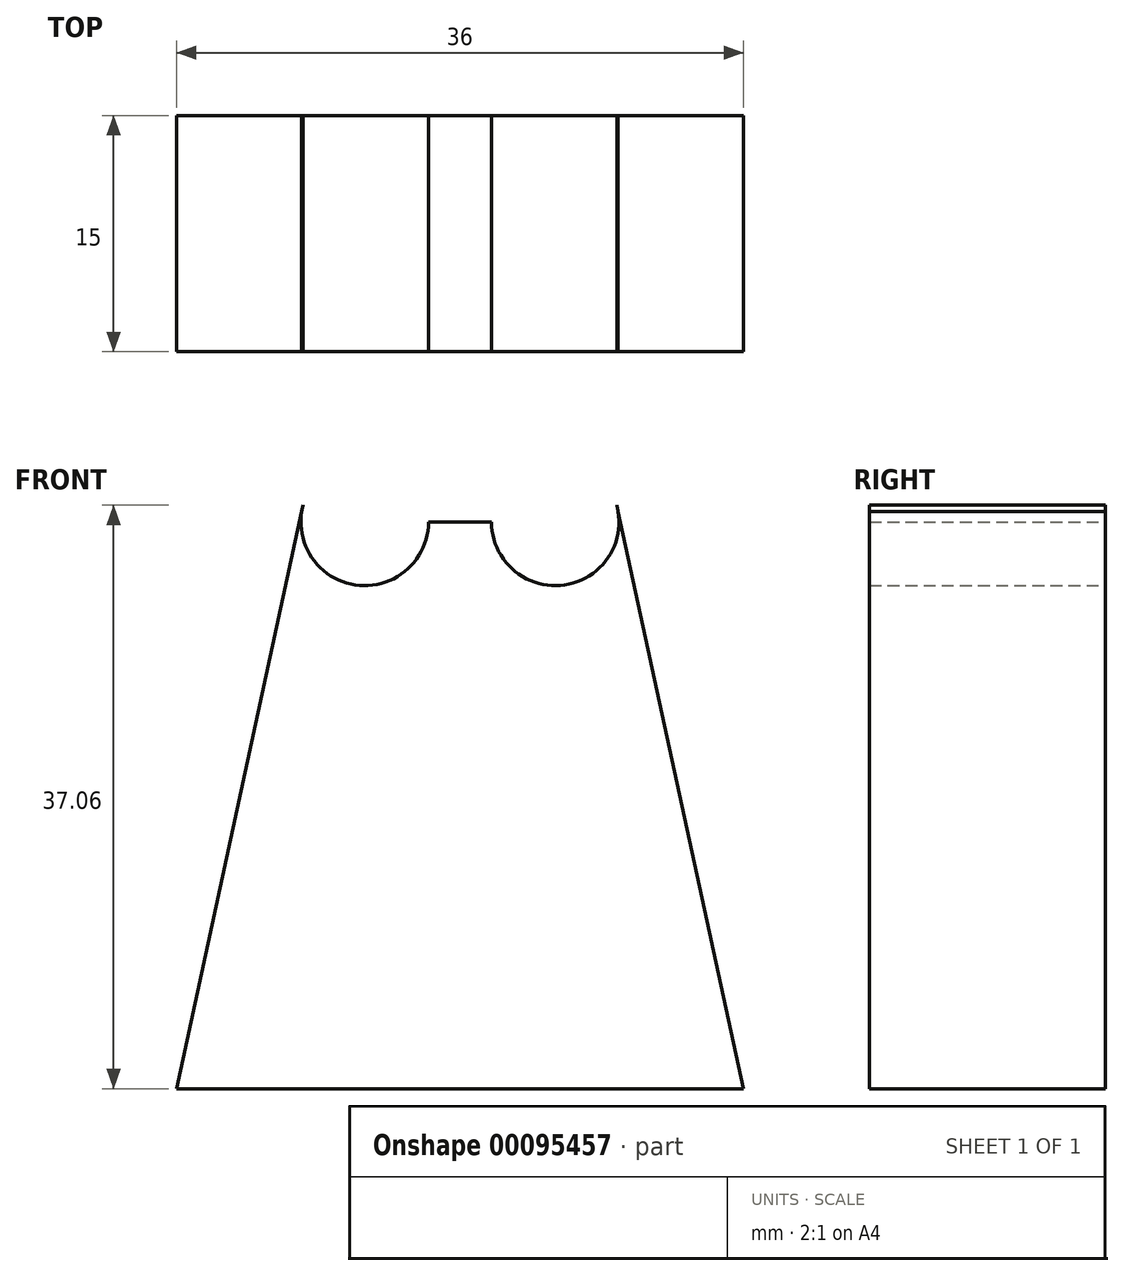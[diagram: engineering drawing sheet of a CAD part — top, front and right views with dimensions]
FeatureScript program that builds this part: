
annotation { "Feature Type Name" : "Feature", "Feature Type Description" : "" }
export const myFeature = defineFeature(function(context is Context, id is Id, definition is map)
    precondition{}
    {
        {
            var Q0;
            Q0=qCreatedBy(makeId("Front.planeOp"),FACE);
            var sketch = newSketch(context, id + "F0", { "sketchPlane" : qUnion([Q0])});
            skArc(sketch, "E0", {"start": v(-27.77, 1.06) * mm, "mid": v(-24.4, -4.01) * mm, "end": v(-19.81, 0) * mm});
            skLineSegment(sketch, "E1", {"start": v(0, 0) * mm, "end": v(-102.74, 0) * mm, "construction": true});
            skLineSegment(sketch, "E2", {"start": v(-27.77, 1.06) * mm, "end": v(-35.81, -36) * mm});
            skLineSegment(sketch, "E3", {"start": v(-35.81, -36) * mm, "end": v(-17.81, -36) * mm});
            skLineSegment(sketch, "E4", {"start": v(-19.81, 0) * mm, "end": v(-17.81, 0) * mm});
            skLineSegment(sketch, "E5", {"start": v(-17.81, 0) * mm, "end": v(-17.81, -36) * mm});
            skLineSegment(sketch, "E6.MirrorCS", {"start": v(-15.81, 0) * mm, "end": v(-17.81, 0) * mm});
            skArc(sketch, "E7.MirrorCS", {"start": v(-7.85, 1.06) * mm, "mid": v(-11.23, -4.01) * mm, "end": v(-15.81, 0) * mm});
            skLineSegment(sketch, "E8.MirrorCS", {"start": v(-7.85, 1.06) * mm, "end": v(0.19, -36) * mm});
            skLineSegment(sketch, "E9.MirrorCS", {"start": v(0.19, -36) * mm, "end": v(-17.81, -36) * mm});
            skSolve(sketch);
        }
        {
            var Q0;
            Q0=qSketchRegion(id+"F0",true);
            extrude(context, id + "F1", {"entities" : qUnion([Q0]), "depth" : 15 * mm});
        }
    });
